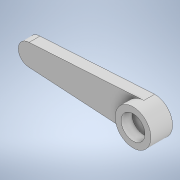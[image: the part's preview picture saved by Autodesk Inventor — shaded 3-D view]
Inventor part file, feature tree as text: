
AUTODESK INVENTOR PART (.ipt)
format: ipt  version: 2021 (Build 250183000, 183)  size: 113,152 bytes
history: native  units: mm
features: extrude x2, sketch x2
ambient origin geometry x8: Origin, YZ Plane, XZ Plane, XY Plane, X Axis, Y Axis, Z Axis, Center Point
bodies: Solid1 (feature_tree)
feature tree (4):
  extrude  "Extrusion1"  Depth=4.0mm
  extrude  "Extrusion2"  Depth=2.0mm TaperAngle=0.0deg
  sketch  "Sketch1"  dims[d0=6.6mm d1=4.0mm]
  sketch  "Sketch2"  dims[d2=21.2mm d3=2.0mm d4=0.0mm d5=4.4mm d6=2.0mm d7=0.0mm]
